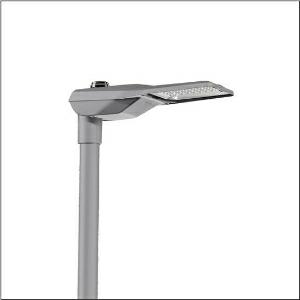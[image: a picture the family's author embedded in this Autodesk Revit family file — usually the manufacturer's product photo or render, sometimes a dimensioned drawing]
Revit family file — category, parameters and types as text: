
# Revit family: streetlight_sl_21_mini___st1_0a_5xe6d47n08hb_a00d
name_source: partatom
category: Lighting Fixtures
units: mm (PartAtom-declared; Revit-internal decimal feet)

## family parameters
Cut with Voids When Loaded = No
Host = Face
Light Source = No
Part Type = Normal
Room Calculation Point = No
Round Connector Dimension = Use Diameter
Shared = No

## types (1)
- --- (1 x LED, 9430 lm, 66 W, 4000K)
    Apparent Load = 66 VA
    CIE Flux Codes = 37 72 97 100 100
    Color Rendering = 70
    Color Temperature = 4000K
    Default Elevation = 1800 mm
    Description = Streetlight SL 21 mini, mast luminaire, primary light control with lens, of PMMA, primary optical cover: cover, of toughened safety glass, transparent, light distribution: ST1.0a, light emission: direct distribution, primary light characteristic: asymmetric, installation type: side-entry, LED, 3G 1.5mm², High Power LED, rated luminous flux: 9.430lm, luminous efficacy: 143lm/W, light colour: 740, colour temperature: 4000K, control gear: NEMA (7pin), control: overheat protection, pre-setting: linear dimming characteristic, constant luminous flux control, time-dependent luminous flux control, flexible luminous flux parameterisation, mains connection: 230..240V, AC, 50/60Hz, connection cable pre-assembled, cable length: 8,5m, wiring characteristics: H07RN-F, start of lifetime: 66W, end of service life: 69W, reduction: 30W, luminaire housing, of diecast aluminium (EN AC-44300), powder-coated, SITECO metallic grey (DB 702S), corrosivity category C5 high according to DIN EN ISO 12944, multi-level sealing system, sealing non-destructively replaceable, inclination adjustable: 0°, 5°, 10°, 15°, length: 628mm, width: 235mm, height: 110mm, spigot size: 42mm (side-entry), mounting height: 4..8m, protection rating (complete): IP66, insulation class (complete): insulation class I (protective earthing), certification: CE, ENEC, ENEC+, VDE, impact resistance: IK10, permissible operating ambient temperature for outdoor applications: -40..+50°C, standard-compliant lighting for roads and squares, packaging unit: 1 piece

Light Distribution: ST1.0a
    Height = 110 mm
    Lamp = 1 x LED
    Lamp Light Flux = 9430 lm
    Lamp Power = 66 W
    Lamp count = 1
    Length = 625 mm
    Luminous efficacy = 143 lm/W
    Manufacturer = Siteco
    ModVariant = No
    Model = 5XE6D47N08HB
    Number of Poles = 1
    OnlyDefault = Yes
    Power Factor = 1
    Product Name = Streetlight SL 21 mini | ST1.0a
    Product group = mast luminaire | pylon top
    ProductGroupID = 6100
    Protection Class = Protection class I
    Protection Degree = IP 66
    RLX_Detail_Level = 1
    RLX_Emergency_Light_Flux = 0 lm
    RLX_Emergency_Type = 0
    RLX_Emergency_Type_DB = No
    RlxData = <blob elided: 26181 chars, md5=e495c9d0>
    Socket = socket
    Standby Power = 0 W
    System Light Flux = 9430 lm
    System Power = 66 W
    Type Comments = factory setting: luminous flux: 100 % | dim-lin: 254 | 670 mA
    Type Image = l_1294379.jpg
    URL = http://relux.com
    VarID = @adj_135699
    Voltage = 0 V
    Weight = 0.00 kg
    Width = 234 mm

## geometry (parser evidence)
native form markers: Blend x4, Sweep x12
no freeform markers — native parametric forms only
